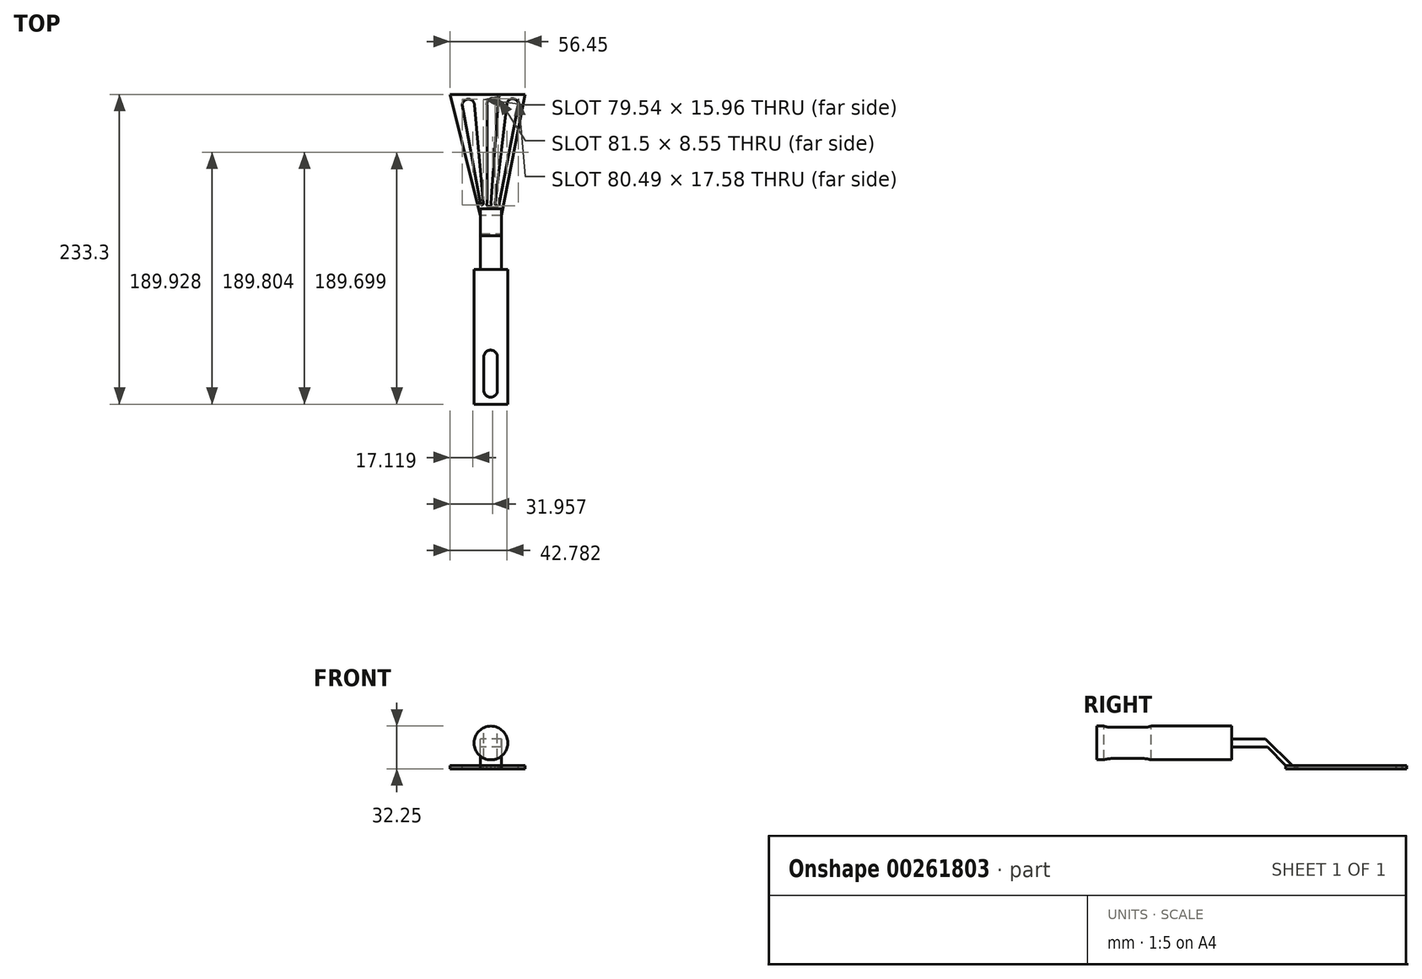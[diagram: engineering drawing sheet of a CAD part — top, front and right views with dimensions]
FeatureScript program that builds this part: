
annotation { "Feature Type Name" : "Feature", "Feature Type Description" : "" }
export const myFeature = defineFeature(function(context is Context, id is Id, definition is map)
    precondition{}
    {
        {
            var Q0;
            Q0=qCreatedBy(makeId("Front.planeOp"),FACE);
            var sketch = newSketch(context, id + "F0", { "sketchPlane" : qUnion([Q0])});
            skCircle(sketch, "E0", {"center": v(0, 0) * mm, "radius": 12.7 * mm});
            skSolve(sketch);
        }
        {
            var Q0;
            Q0=makeQuery(id+"F0.imprint","IMPRINT",FACE,{"disambiguationData":[TD([[makeQuery(id+"F0.imprint","IMPRINT",EDGE,{"derivedFrom":sQuery(id+"F0.wireOp",EDGE,"E0")}),1.0]])]});
            extrude(context, id + "F1", {"entities" : qUnion([Q0]), "depth" : 101.6 * mm});
        }
        {
            var Q0;
            Q0=qCreatedBy(makeId("Top.planeOp"),FACE);
            var sketch = newSketch(context, id + "F2", { "sketchPlane" : qUnion([Q0])});
            skLineSegment(sketch, "E1", {"start": v(-5.35, -91.32) * mm, "end": v(-5.35, -65.89) * mm});
            skLineSegment(sketch, "E2", {"start": v(4.81, -91.29) * mm, "end": v(4.81, -65.89) * mm});
            skArc(sketch, "E3", {"start": v(-5.35, -91.32) * mm, "mid": v(-0.25, -96.37) * mm, "end": v(4.81, -91.29) * mm});
            skArc(sketch, "E4", {"start": v(4.81, -65.89) * mm, "mid": v(-0.27, -60.83) * mm, "end": v(-5.35, -65.89) * mm});
            skSolve(sketch);
        }
        {
            var Q0;
            Q0 = qSketchRegion(id + "F2", true);
            var Q1;
            Q1=makeQuery(id+"F1.opExtrude","SWEPT_FACE",FACE,{"disambiguationData":[OSD([sQuery(id+"F0.wireOp",EDGE,"E0")])]});
            extrude(context, id + "F3", {"entities" : qUnion([Q0]), "operationType" : NewBodyOperationType.REMOVE, "endBound" : BoundingType.SYMMETRIC, "oppositeDirection" : true, "endBoundEntityFace" : qUnion([Q1]), "depth" : 25.4 * mm});
        }
        {
            var Q0;
            Q0=makeQuery(id+"F1.opExtrude","CAP_FACE",FACE,{"disambiguationData":[OSD([sQuery(id+"F0.wireOp",EDGE,"E0")])],"isStart":true});
            var sketch = newSketch(context, id + "F4", { "sketchPlane" : qUnion([Q0])});
            skLineSegment(sketch, "E5.bottom", {"start": v(-8.02, -3.16) * mm, "end": v(8.02, -3.16) * mm});
            skLineSegment(sketch, "E5.top", {"start": v(-8.02, 3.16) * mm, "end": v(8.02, 3.16) * mm});
            skLineSegment(sketch, "E5.left", {"start": v(-8.02, -3.16) * mm, "end": v(-8.02, 3.16) * mm});
            skLineSegment(sketch, "E5.right", {"start": v(8.02, -3.16) * mm, "end": v(8.02, 3.16) * mm});
            skPoint(sketch, "E5.middle", {"position": v(0, 0) * mm});
            skSolve(sketch);
        }
        {
            var Q0;
            Q0 = qSketchRegion(id + "F4", true);
            extrude(context, id + "F5", {"entities" : qUnion([Q0]), "operationType" : NewBodyOperationType.ADD, "depth" : 25.4 * mm});
        }
        {
            var Q0;
            Q0=makeQuery(id+"F5.opExtrude","CAP_FACE",FACE,{"disambiguationData":[OSD([sQuery(id+"F4.wireOp",EDGE,"E5.bottom"),sQuery(id+"F4.wireOp",EDGE,"E5.top"),sQuery(id+"F4.wireOp",EDGE,"E5.left"),sQuery(id+"F4.wireOp",EDGE,"E5.right")])],"isStart":false});
            var sketch = newSketch(context, id + "F6", { "sketchPlane" : qUnion([Q0])});
            skLineSegment(sketch, "E6", {"start": v(-8.02, 3.16) * mm, "end": v(-8.02, -17) * mm});
            skPoint(sketch, "E6.endSnap0", {"position": v(-8.02, 0) * mm});
            skLineSegment(sketch, "E7", {"start": v(-8.02, -17) * mm, "end": v(-8.02, 3.16) * mm});
            skLineSegment(sketch, "E8", {"start": v(8.02, 3.16) * mm, "end": v(8.02, -17) * mm});
            skLineSegment(sketch, "E9", {"start": v(8.02, -17) * mm, "end": v(-8.02, -17) * mm});
            skLineSegment(sketch, "E10", {"start": v(-8.02, 3.16) * mm, "end": v(8.02, 3.16) * mm});
            skSolve(sketch);
        }
        {
            var Q0;
            Q0 = qSketchRegion(id + "F6", true);
            extrude(context, id + "F7", {"entities" : qUnion([Q0]), "operationType" : NewBodyOperationType.ADD, "depth" : 25.4 * mm});
        }
        {
            var Q0;
            Q0=makeQuery(id+"F7.opExtrude","CAP_EDGE",EDGE,{"disambiguationData":[OSD([sQuery(id+"F6.wireOp",EDGE,"E10")])],"isStart":false});
            chamfer(context, id + "F8", {"entities" : qUnion([Q0]), "width" : 25.4 * mm, "tangentPropagation" : true});
        }
        {
            var Q0;
            Q0=makeQuery(id+"F7.opExtrude","CAP_EDGE",EDGE,{"disambiguationData":[OSD([sQuery(id+"F6.wireOp",EDGE,"E9")])],"isStart":true});
            chamfer(context, id + "F9", {"entities" : qUnion([Q0]), "width" : 15.24 * mm, "tangentPropagation" : true});
        }
        {
            var Q0;
            Q0=makeQuery(id+"F7.opExtrude","SWEPT_FACE",FACE,{"disambiguationData":[OSD([sQuery(id+"F6.wireOp",EDGE,"E9")])]});
            var sketch = newSketch(context, id + "F10", { "sketchPlane" : qUnion([Q0])});
            skLineSegment(sketch, "E11", {"start": v(8.02, -40.64) * mm, "end": v(25.62, -131.7) * mm});
            skLineSegment(sketch, "E12", {"start": v(-8.02, -40.64) * mm, "end": v(-30.83, -131.7) * mm});
            skLineSegment(sketch, "E13", {"start": v(-30.83, -131.7) * mm, "end": v(25.62, -131.7) * mm});
            skLineSegment(sketch, "E14", {"start": v(8.02, -40.64) * mm, "end": v(-8.02, -40.64) * mm});
            skSolve(sketch);
        }
        {
            var Q0;
            Q0 = qSketchRegion(id + "F10", true);
            extrude(context, id + "F11", {"entities" : qUnion([Q0]), "depth" : 2.54 * mm});
        }
        {
            var Q0;
            Q0=makeQuery(id+"F11.opExtrude","CAP_FACE",FACE,{"disambiguationData":[OSD([sQuery(id+"F10.wireOp",EDGE,"E11"),sQuery(id+"F10.wireOp",EDGE,"E12"),sQuery(id+"F10.wireOp",EDGE,"E13"),sQuery(id+"F10.wireOp",EDGE,"E14")])],"isStart":true});
            var sketch = newSketch(context, id + "F12", { "sketchPlane" : qUnion([Q0])});
            skLineSegment(sketch, "E15", {"start": v(0, 49.8) * mm, "end": v(5.4, 124.33) * mm});
            skLineSegment(sketch, "E16", {"start": v(-2.95, 49.8) * mm, "end": v(-2.95, 123.8) * mm});
            skLineSegment(sketch, "E17", {"start": v(-5.73, 49.8) * mm, "end": v(-12.29, 123.8) * mm});
            skLineSegment(sketch, "E18", {"start": v(-8.02, 49.8) * mm, "end": v(-21.7, 123.8) * mm});
            skArc(sketch, "E19", {"start": v(-12.29, 123.8) * mm, "mid": v(-16.99, 128.1) * mm, "end": v(-21.7, 123.8) * mm});
            skArc(sketch, "E20", {"start": v(-8.02, 49.8) * mm, "mid": v(-6.88, 48.56) * mm, "end": v(-5.73, 49.8) * mm});
            skArc(sketch, "E21", {"start": v(5.4, 124.33) * mm, "mid": v(0.92, 128.85) * mm, "end": v(-2.95, 123.8) * mm});
            skArc(sketch, "E22", {"start": v(-2.95, 49.8) * mm, "mid": v(-1.48, 47.35) * mm, "end": v(0, 49.8) * mm});
            skLineSegment(sketch, "E23", {"start": v(20.74, 124) * mm, "end": v(6.43, 49.93) * mm});
            skLineSegment(sketch, "E24", {"start": v(3.16, 49.8) * mm, "end": v(12, 124.59) * mm});
            skArc(sketch, "E25", {"start": v(20.74, 124) * mm, "mid": v(16.65, 128.45) * mm, "end": v(12, 124.59) * mm});
            skArc(sketch, "E26", {"start": v(3.16, 49.8) * mm, "mid": v(4.87, 47.96) * mm, "end": v(6.43, 49.93) * mm});
            skSolve(sketch);
        }
        {
            var Q0;
            Q0 = qSketchRegion(id + "F12", true);
            extrude(context, id + "F13", {"entities" : qUnion([Q0]), "operationType" : NewBodyOperationType.REMOVE, "oppositeDirection" : true, "depth" : 2.54 * mm});
        }
    });
